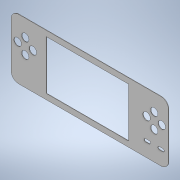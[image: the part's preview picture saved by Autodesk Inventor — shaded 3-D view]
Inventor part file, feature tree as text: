
AUTODESK INVENTOR PART (.ipt)
format: ipt  version: 2022 (Build 260153000, 153)  size: 160,768 bytes
history: native  units: mm
features: extrude x1, sketch x1
ambient origin geometry x8: Origin, YZ Plane, XZ Plane, XY Plane, X Axis, Y Axis, Z Axis, Center Point
bodies: 实体1 (feature_tree)
feature tree (2):
  extrude  "拉伸1"  Depth=8.0mm
  sketch  "草图1"  dims[d12=2.0mm d13=2.0mm d23=169.95mm d24=64.95mm d25=7.1mm d26=3.1mm d27=7.1mm d28=3.1mm d29=8.0mm d30=88.55mm d34=53.24mm d35=8.1mm d36=8.1mm d37=8.1mm d38=8.1mm d39=8.1mm d40=8.1mm d41=8.1mm d42=8.1mm d43=0.5mm d44=0.0mm]
